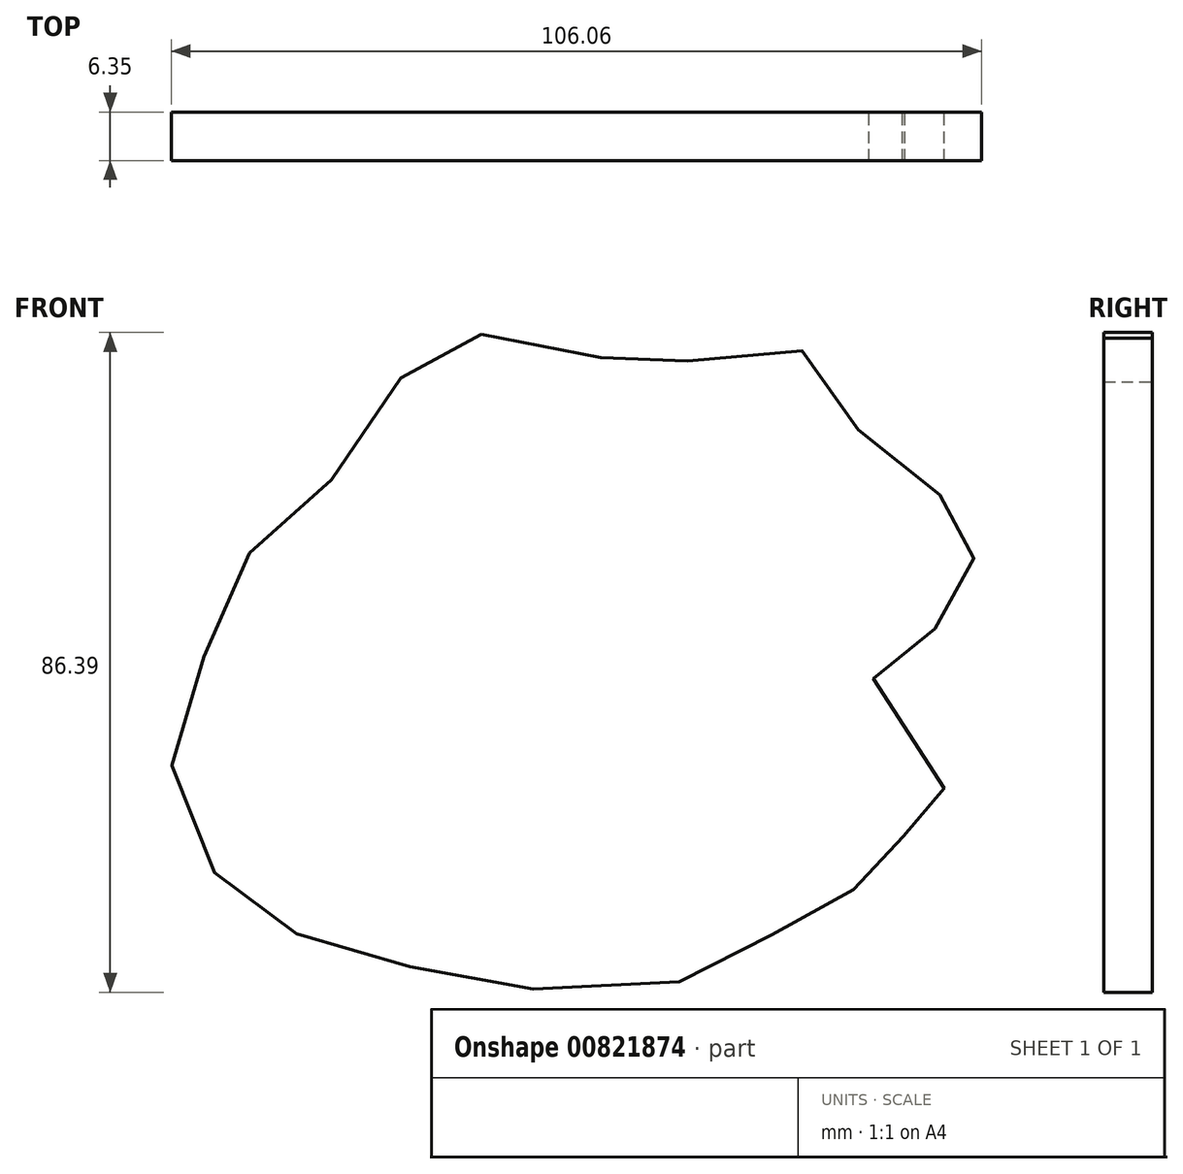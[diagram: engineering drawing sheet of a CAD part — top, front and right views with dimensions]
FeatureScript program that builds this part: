
annotation { "Feature Type Name" : "Feature", "Feature Type Description" : "" }
export const myFeature = defineFeature(function(context is Context, id is Id, definition is map)
    precondition{}
    {
        {
            var Q0;
            Q0=qCreatedBy(makeId("Front.planeOp"),FACE);
            var sketch = newSketch(context, id + "F0", { "sketchPlane" : qUnion([Q0])});
            skFitSpline(sketch, "E0", {"points": [v(-12.48, 54.51) * mm, v(-20.3, 51.78) * mm, v(-25.76, 44.55) * mm, v(-34.75, 32.63) * mm, v(-42.57, 26.18) * mm, v(-46.86, 16.22) * mm, v(-52.33, 4.69) * mm, v(-52.14, -6.45) * mm, v(-46.47, -17.2) * mm, v(-39.05, -22.86) * mm, v(-28.7, -26.77) * mm, v(-14.63, -29.7) * mm, v(0, -31.65) * mm, v(18.4, -28.72) * mm, v(25.04, -24.42) * mm, v(34.22, -20.32) * mm, v(37.35, -17.2) * mm, v(42.82, -13.48) * mm, v(42.82, -9.57) * mm, v(47.31, -7.62) * mm, v(45.94, 0) * mm, v(38.32, 11.72) * mm, v(45.16, 15.44) * mm, v(49.85, 18.17) * mm, v(52, 25.2) * mm, v(52.98, 26.18) * mm, v(48.87, 32.43) * mm, v(37.54, 40.05) * mm, v(36.57, 43.77) * mm, v(30.31, 51.78) * mm, v(19.57, 53.34) * mm, v(7.26, 48.26) * mm, v(1.79, 52.56) * mm, v(-12.48, 54.51) * mm]});
            skSolve(sketch);
        }
        {
            var Q0;
            Q0 = qSketchRegion(id + "F0", true);
            extrude(context, id + "F1", {"entities" : qUnion([Q0]), "depth" : 6.35 * mm, "offsetDistance" : 25.4 * mm});
        }
    });
